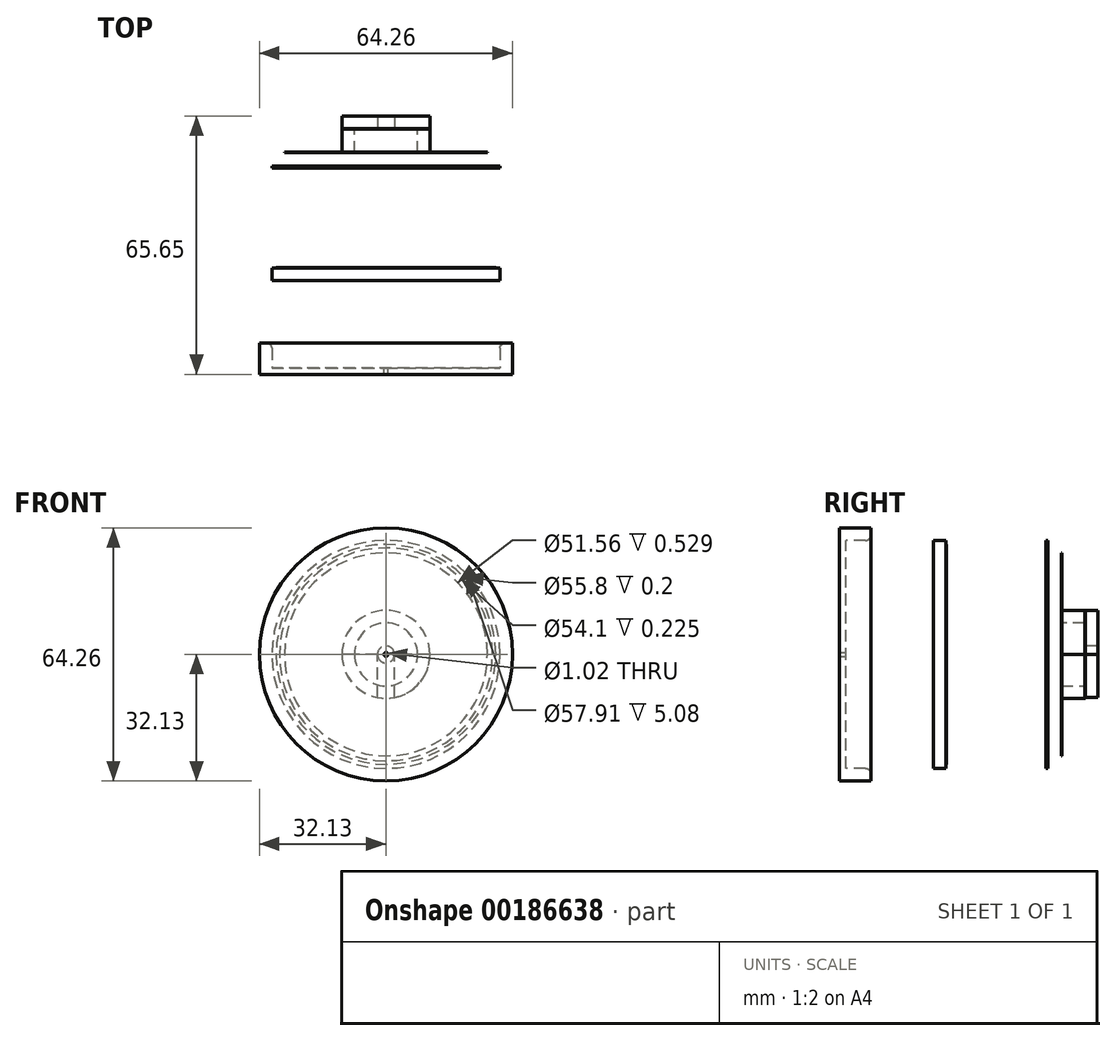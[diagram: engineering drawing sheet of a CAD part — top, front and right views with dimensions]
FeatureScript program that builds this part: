
annotation { "Feature Type Name" : "Feature", "Feature Type Description" : "" }
export const myFeature = defineFeature(function(context is Context, id is Id, definition is map)
    precondition{}
    {
        {
            assignVariable(context, id + "F0", {"name" : "Ant_Thick", "anyValue" : 1 / 8});
        }
        {
            assignVariable(context, id + "F1", {"name" : "SHIELD_Thick", "anyValue" : .1});
        }
        {
            assignVariable(context, id + "F2", {"name" : "tolerance", "anyValue" : 0});
        }
        {
            assignVariable(context, id + "F3", {"name" : "Layers_SH", "anyValue" : 4});
        }
        {
            assignVariable(context, id + "F4", {"name" : "LID_FOLD_DEPTH", "anyValue" : .2});
        }
        {
            assignVariable(context, id + "F5", {"name" : "TOT_SH_SPACE", "anyValue" : getVariable(context, 'SHIELD_Thick') * getVariable(context, 'Layers_SH') + getVariable(context, 'tolerance')});
        }
        {
            var Q0;
            Q0=qCreatedBy(makeId("Front.planeOp"),FACE);
            var sketch = newSketch(context, id + "F6", { "sketchPlane" : qUnion([Q0])});
            skCircle(sketch, "E0", {"center": v(0, 0) * mm, "radius": 25.78 * mm});
            skLineSegment(sketch, "E1", {"start": v(0, 28.96) * mm, "end": v(0, -28.96) * mm, "construction": true});
            skLineSegment(sketch, "E2", {"start": v(28.96, 0) * mm, "end": v(-28.96, 0) * mm, "construction": true});
            skCircle(sketch, "E3.0", {"center": v(0, 0) * mm, "radius": 28.96 * mm});
            skCircle(sketch, "E4", {"center": v(0, 0) * mm, "radius": 24.77 * mm, "construction": true});
            skCircle(sketch, "E5", {"center": v(0, 0) * mm, "radius": 8 * mm});
            skCircle(sketch, "E6", {"center": v(0, 0) * mm, "radius": 6.99 * mm, "construction": true});
            skCircle(sketch, "E7", {"center": v(0, 0) * mm, "radius": 2.16 * mm});
            skCircle(sketch, "E8.0", {"center": v(0, 0) * mm, "radius": 11.18 * mm});
            skLineSegment(sketch, "E9", {"start": v(11.18, 0) * mm, "end": v(-11.18, 0) * mm});
            skCircle(sketch, "E10.0", {"center": v(0, 0) * mm, "radius": 27.05 * mm});
            skCircle(sketch, "E11", {"center": v(0, 0) * mm, "radius": 27.9 * mm});
            skCircle(sketch, "E12", {"center": v(0, 0) * mm, "radius": 27.64 * mm, "construction": true});
            skSolve(sketch);
        }
        {
            var Q0;
            Q0=makeQuery(id+"F6.imprint","IMPRINT",FACE,{"disambiguationData":[TD([[makeQuery(id+"F6.imprint","IMPRINT",EDGE,{"derivedFrom":sQuery(id+"F6.wireOp",EDGE,"E0")}),-1.0]])]});
            var Q1;
            Q1=makeQuery(id+"F6.imprint","IMPRINT",FACE,{"disambiguationData":[TD([[makeQuery(id+"F6.imprint","IMPRINT",EDGE,{"derivedFrom":sQuery(id+"F6.wireOp",EDGE,"E3.0")}),1.0]])]});
            var Q2;
            Q2=makeQuery(id+"F6.imprint","IMPRINT",FACE,{"disambiguationData":[TD([[makeQuery(id+"F6.imprint","IMPRINT",EDGE,{"derivedFrom":sQuery(id+"F6.wireOp",EDGE,"E10.0")}),-1.0]])]});
            extrude(context, id + "F7", {"entities" : qUnion([Q0, Q1, Q2]), "depth" : (3.56 + getVariable(context, 'Ant_Thick') + (getVariable(context, 'Layers_SH') * getVariable(context, 'SHIELD_Thick') + getVariable(context, 'tolerance'))) * mm});
        }
        {
            var Q0;
            {var subQ0=sQuery(id+"F6.wireOp",EDGE,"E9");var subQ1=sQuery(id+"F6.wireOp",EDGE,"E5");var subQ2=makeQuery(id+"F6.imprint","INTERSECT",VERTEX,{"disambiguationData":[OD(0.0)],"derivedFrom":[subQ1,subQ0]});Q0=makeQuery(id+"F6.imprint","IMPRINT",FACE,{"disambiguationData":[TD([[makeQuery(id+"F6.imprint","IMPRINT",EDGE,{"disambiguationData":[TD([[subQ2,1.0]])],"derivedFrom":subQ1}),-1.0]])]});}
            var Q1;
            Q1=makeQuery(id+"F6.imprint","IMPRINT",FACE,{"disambiguationData":[TD([[makeQuery(id+"F6.imprint","IMPRINT",EDGE,{"derivedFrom":sQuery(id+"F6.wireOp",EDGE,"E0")}),-1.0]])]});
            var Q2;
            Q2=makeQuery(id+"F6.imprint","IMPRINT",FACE,{"disambiguationData":[TD([[makeQuery(id+"F6.imprint","IMPRINT",EDGE,{"derivedFrom":sQuery(id+"F6.wireOp",EDGE,"E0")}),1.0]])]});
            extrude(context, id + "F8", {"entities" : qUnion([Q0, Q1, Q2]), "depth" : (getVariable(context, 'Ant_Thick')) * mm});
        }
        {
            var Q0;
            {var subQ0=sQuery(id+"F6.wireOp",EDGE,"E9");var subQ1=sQuery(id+"F6.wireOp",EDGE,"E5");var subQ2=makeQuery(id+"F6.imprint","INTERSECT",VERTEX,{"disambiguationData":[OD(0.0)],"derivedFrom":[subQ1,subQ0]});Q0=makeQuery(id+"F6.imprint","IMPRINT",FACE,{"disambiguationData":[TD([[makeQuery(id+"F6.imprint","IMPRINT",EDGE,{"disambiguationData":[TD([[subQ2,1.0]])],"derivedFrom":subQ1}),-1.0]])]});}
            extrude(context, id + "F9", {"entities" : qUnion([Q0]), "operationType" : NewBodyOperationType.ADD, "oppositeDirection" : true, "depth" : (6 - getVariable(context, 'Ant_Thick')) * mm});
        }
        {
            var Q0;
            Q0=makeQuery(id+"F9.opExtrude","CAP_FACE",FACE,{"disambiguationData":[OSD([sQuery(id+"F6.wireOp",EDGE,"E5"),sQuery(id+"F6.wireOp",EDGE,"E8.0")])],"isStart":false});
            var sketch = newSketch(context, id + "F10", { "sketchPlane" : qUnion([Q0])});
            skCircle(sketch, "E13", {"center": v(0, 0) * mm, "radius": 2.16 * mm});
            skCircle(sketch, "E14", {"center": v(0, 0) * mm, "radius": 8 * mm});
            skCircle(sketch, "E15", {"center": v(0, 0) * mm, "radius": 11.18 * mm});
            skLineSegment(sketch, "E16", {"start": v(-11.18, 0) * mm, "end": v(11.18, 0) * mm});
            skSolve(sketch);
        }
        {
            var Q0;
            {var subQ0=sQuery(id+"F10.wireOp",EDGE,"E14");Q0=makeQuery(id+"F10.imprint","IMPRINT",FACE,{"disambiguationData":[TD([[makeQuery(id+"F10.imprint","IMPRINT",EDGE,{"disambiguationData":[OD(1.0)],"derivedFrom":subQ0}),1.0]])]});}
            var Q1;
            {var subQ4=sQuery(id+"F10.wireOp",EDGE,"E14");Q1=makeQuery(id+"F10.imprint","IMPRINT",FACE,{"disambiguationData":[TD([[makeQuery(id+"F10.imprint","IMPRINT",EDGE,{"disambiguationData":[OD(1.0)],"derivedFrom":subQ4}),-1.0]])]});}
            var Q2;
            {var subQ0=sQuery(id+"F10.wireOp",EDGE,"E14");Q2=makeQuery(id+"F10.imprint","IMPRINT",FACE,{"disambiguationData":[TD([[makeQuery(id+"F10.imprint","IMPRINT",EDGE,{"disambiguationData":[OD(1.0)],"derivedFrom":subQ0}),1.0]])]});}
            extrude(context, id + "F11", {"entities" : qUnion([Q0, Q1, Q2]), "depth" : (getVariable(context, 'Ant_Thick')) * mm});
        }
        {
            var Q0;
            {var subQ0=sQuery(id+"F6.wireOp",EDGE,"E9");var subQ1=sQuery(id+"F6.wireOp",EDGE,"E5");var subQ2=makeQuery(id+"F6.imprint","INTERSECT",VERTEX,{"disambiguationData":[OD(0.0)],"derivedFrom":[subQ1,subQ0]});Q0=makeQuery(id+"F6.imprint","IMPRINT",FACE,{"disambiguationData":[TD([[makeQuery(id+"F6.imprint","IMPRINT",EDGE,{"disambiguationData":[TD([[subQ2,-1.0]])],"derivedFrom":subQ1}),-1.0]])]});}
            var Q1;
            Q1=makeQuery(id+"F9.opExtrude","CAP_FACE",FACE,{"disambiguationData":[OSD([sQuery(id+"F6.wireOp",EDGE,"E5"),sQuery(id+"F6.wireOp",EDGE,"E8.0"),sQuery(id+"F6.wireOp",EDGE,"E9")])],"isStart":false});
            var Q2;
            Q2=makeQuery(id+"F8.opExtrude","CAP_FACE",FACE,{"disambiguationData":[OSD([sQuery(id+"F6.wireOp",EDGE,"E3.0"),sQuery(id+"F6.wireOp",EDGE,"E5"),sQuery(id+"F6.wireOp",EDGE,"E8.0"),sQuery(id+"F6.wireOp",EDGE,"E9")])],"isStart":false});
            extrude(context, id + "F12", {"entities" : qUnion([Q0]), "endBound" : BoundingType.UP_TO_SURFACE, "oppositeDirection" : true, "endBoundEntityFace" : qUnion([Q1]), "depth" : 25.4 * mm, "hasSecondDirection" : true, "secondDirectionBound" : SecondDirectionBoundingType.UP_TO_SURFACE, "secondDirectionOppositeDirection" : false, "secondDirectionBoundEntityFace" : qUnion([Q2]), "secondDirectionDepth" : 25.4 * mm});
        }
        {
            var Q0;
            {var subQ0=sQuery(id+"F10.wireOp",EDGE,"E14");Q0=makeQuery(id+"F10.imprint","IMPRINT",FACE,{"disambiguationData":[TD([[makeQuery(id+"F10.imprint","IMPRINT",EDGE,{"disambiguationData":[OD(0.0)],"derivedFrom":subQ0}),-1.0]])]});}
            var Q1;
            {var subQ4=sQuery(id+"F10.wireOp",EDGE,"E14");Q1=makeQuery(id+"F10.imprint","IMPRINT",FACE,{"disambiguationData":[TD([[makeQuery(id+"F10.imprint","IMPRINT",EDGE,{"disambiguationData":[OD(0.0)],"derivedFrom":subQ4}),1.0]])]});}
            var Q2;
            Q2=makeQuery(id+"F11.opExtrude","CAP_FACE",FACE,{"disambiguationData":[OSD([sQuery(id+"F10.wireOp",EDGE,"E13"),sQuery(id+"F10.wireOp",EDGE,"E15"),sQuery(id+"F10.wireOp",EDGE,"E16")])],"isStart":false});
            extrude(context, id + "F13", {"entities" : qUnion([Q0, Q1]), "endBoundEntityFace" : qUnion([Q2]), "depth" : (getVariable(context, 'Ant_Thick')) * mm});
        }
        {
            var Q0;
            Q0=makeQuery(id+"F13.opExtrude","CAP_FACE",FACE,{"disambiguationData":[OSD([sQuery(id+"F10.wireOp",EDGE,"E13"),sQuery(id+"F10.wireOp",EDGE,"E15"),sQuery(id+"F10.wireOp",EDGE,"E16")])],"isStart":false});
            extrude(context, id + "F14", {"entities" : qUnion([Q0]), "depth" : 3.17 * mm});
        }
        {
            var Q0;
            {var subQ0=sQuery(id+"F10.wireOp",EDGE,"E16");var subQ1=makeQuery(id+"F10.imprint","INTERSECT",VERTEX,{"disambiguationData":[OD(1.0)],"derivedFrom":[sQuery(id+"F10.wireOp",EDGE,"E14"),subQ0]});Q0=makeQuery(id+"F14.opExtrude","SWEPT_FACE",FACE,{"disambiguationData":[OSD([subQ0]),TDD([makeQuery(id+"F13.opExtrude","CAP_EDGE",EDGE,{"disambiguationData":[OSD([subQ0]),TDD([makeQuery(id+"F10.imprint","IMPRINT",EDGE,{"disambiguationData":[TD([[subQ1,1.0]])],"derivedFrom":subQ0}),makeQuery(id+"F10.imprint","IMPRINT",EDGE,{"disambiguationData":[TD([[makeQuery(id+"F10.imprint","INTERSECT",VERTEX,{"disambiguationData":[OD(1.0)],"derivedFrom":[sQuery(id+"F10.wireOp",EDGE,"E15"),subQ0]}),1.0]])],"derivedFrom":subQ0})])],"isStart":false})])]});}
            var Q1;
            {var subQ0=sQuery(id+"F10.wireOp",EDGE,"E16");var subQ1=makeQuery(id+"F10.imprint","INTERSECT",VERTEX,{"disambiguationData":[OD(0.0)],"derivedFrom":[sQuery(id+"F10.wireOp",EDGE,"E14"),subQ0]});Q1=makeQuery(id+"F14.opExtrude","SWEPT_FACE",FACE,{"disambiguationData":[OSD([subQ0]),TDD([makeQuery(id+"F13.opExtrude","CAP_EDGE",EDGE,{"disambiguationData":[OSD([subQ0]),TDD([makeQuery(id+"F10.imprint","IMPRINT",EDGE,{"disambiguationData":[TD([[makeQuery(id+"F10.imprint","INTERSECT",VERTEX,{"disambiguationData":[OD(0.0)],"derivedFrom":[sQuery(id+"F10.wireOp",EDGE,"E15"),subQ0]}),-1.0]])],"derivedFrom":subQ0}),makeQuery(id+"F10.imprint","IMPRINT",EDGE,{"disambiguationData":[TD([[subQ1,-1.0]])],"derivedFrom":subQ0})])],"isStart":false})])]});}
            var Q2;
            Q2=makeQuery(id+"F11.opExtrude","SWEPT_FACE",FACE,{"disambiguationData":[OSD([sQuery(id+"F10.wireOp",EDGE,"E15")])]});
            extrude(context, id + "F15", {"entities" : qUnion([Q0, Q1]), "endBound" : BoundingType.UP_TO_SURFACE, "endBoundEntityFace" : qUnion([Q2]), "depth" : 25.4 * mm});
        }
        {
            var Q0;
            Q0=qCreatedBy(makeId("Front.planeOp"),FACE);
            cPlane(context, id + "F16", {"entities" : qUnion([Q0]), "cplaneType" : CPlaneType.OFFSET, "offset" : (getVariable(context, 'Ant_Thick')) * mm, "width" : 152.4 * mm, "height" : 152.4 * mm});
        }
        {
            var Q0;
            Q0=makeQuery(id+"F7.opExtrude","CAP_FACE",FACE,{"disambiguationData":[OSD([sQuery(id+"F6.wireOp",EDGE,"E0"),sQuery(id+"F6.wireOp",EDGE,"E3.0")])],"isStart":false});
            cPlane(context, id + "F17", {"entities" : qUnion([Q0]), "cplaneType" : CPlaneType.OFFSET, "offset" : 25.4 * mm, "width" : 152.4 * mm, "height" : 152.4 * mm});
        }
        {
            var Q0;
            Q0=qCreatedBy(id+"F17.planeOp",FACE);
            var sketch = newSketch(context, id + "F18", { "sketchPlane" : qUnion([Q0])});
            skCircle(sketch, "E17", {"center": v(0, 0) * mm, "radius": 28.96 * mm});
            skCircle(sketch, "E18", {"center": v(0, 0) * mm, "radius": 24.77 * mm});
            skCircle(sketch, "E19", {"center": v(0, 0) * mm, "radius": 27.9 * mm});
            skCircle(sketch, "E20", {"center": v(0, 0) * mm, "radius": 27.05 * mm});
            skSolve(sketch);
        }
        {
            var Q0;
            Q0=makeQuery(id+"F18.imprint","IMPRINT",FACE,{"disambiguationData":[TD([[makeQuery(id+"F18.imprint","IMPRINT",EDGE,{"derivedFrom":sQuery(id+"F18.wireOp",EDGE,"E17")}),1.0]])]});
            var Q1;
            Q1=makeQuery(id+"F18.imprint","IMPRINT",FACE,{"disambiguationData":[TD([[makeQuery(id+"F18.imprint","IMPRINT",EDGE,{"derivedFrom":sQuery(id+"F18.wireOp",EDGE,"E18")}),1.0]])]});
            var Q2;
            Q2=makeQuery(id+"F18.imprint","IMPRINT",FACE,{"disambiguationData":[TD([[makeQuery(id+"F18.imprint","IMPRINT",EDGE,{"derivedFrom":sQuery(id+"F18.wireOp",EDGE,"E18")}),-1.0]])]});
            var Q3;
            Q3=makeQuery(id+"F18.imprint","IMPRINT",FACE,{"disambiguationData":[TD([[makeQuery(id+"F18.imprint","IMPRINT",EDGE,{"derivedFrom":sQuery(id+"F18.wireOp",EDGE,"E19")}),1.0]])]});
            extrude(context, id + "F19", {"entities" : qUnion([Q0, Q1, Q2, Q3]), "depth" : 3.17 * mm});
        }
        {
            var Q0;
            Q0=makeQuery(id+"F18.imprint","IMPRINT",FACE,{"disambiguationData":[TD([[makeQuery(id+"F18.imprint","IMPRINT",EDGE,{"derivedFrom":sQuery(id+"F18.wireOp",EDGE,"E18")}),1.0]])]});
            var Q1;
            Q1=makeQuery(id+"F18.imprint","IMPRINT",FACE,{"disambiguationData":[TD([[makeQuery(id+"F18.imprint","IMPRINT",EDGE,{"derivedFrom":sQuery(id+"F18.wireOp",EDGE,"E18")}),-1.0]])]});
            extrude(context, id + "F20", {"entities" : qUnion([Q0, Q1]), "oppositeDirection" : true, "depth" : (getVariable(context, 'Ant_Thick')) * mm});
        }
        {
            var Q0;
            Q0=makeQuery(id+"F7.opExtrude","CAP_FACE",FACE,{"disambiguationData":[OSD([sQuery(id+"F6.wireOp",EDGE,"E0"),sQuery(id+"F6.wireOp",EDGE,"E3.0")])],"isStart":false});
            var sketch = newSketch(context, id + "F21", { "sketchPlane" : qUnion([Q0])});
            skCircle(sketch, "E21", {"center": v(0, 0) * mm, "radius": 27.05 * mm});
            skCircle(sketch, "E22", {"center": v(0, 0) * mm, "radius": 27.64 * mm});
            skCircle(sketch, "E23", {"center": v(0, 0) * mm, "radius": 27.9 * mm});
            skSolve(sketch);
        }
        {
            var Q0;
            Q0=makeQuery(id+"F21.imprint","IMPRINT",FACE,{"disambiguationData":[TD([[makeQuery(id+"F21.imprint","IMPRINT",EDGE,{"derivedFrom":sQuery(id+"F21.wireOp",EDGE,"E22")}),-1.0]])]});
            var Q1;
            Q1=makeQuery(id+"F21.imprint","IMPRINT",FACE,{"disambiguationData":[TD([[makeQuery(id+"F21.imprint","IMPRINT",EDGE,{"derivedFrom":sQuery(id+"F21.wireOp",EDGE,"E21")}),-1.0]])]});
            extrude(context, id + "F22", {"entities" : qUnion([Q0, Q1]), "operationType" : NewBodyOperationType.REMOVE, "oppositeDirection" : true, "depth" : (getVariable(context, 'LID_FOLD_DEPTH')) * mm});
        }
        {
            var Q0;
            Q0=makeQuery(id+"F18.imprint","IMPRINT",FACE,{"disambiguationData":[TD([[makeQuery(id+"F18.imprint","IMPRINT",EDGE,{"derivedFrom":sQuery(id+"F18.wireOp",EDGE,"E19")}),1.0]])]});
            extrude(context, id + "F23", {"entities" : qUnion([Q0]), "oppositeDirection" : true, "depth" : (getVariable(context, 'Ant_Thick') + .1) * mm});
        }
        {
            var Q0;
            Q0=qCreatedBy(id+"F16.planeOp",FACE);
            var sketch = newSketch(context, id + "F24", { "sketchPlane" : qUnion([Q0])});
            skCircle(sketch, "E24", {"center": v(0, 0) * mm, "radius": 27.9 * mm});
            skCircle(sketch, "E25", {"center": v(0, 0) * mm, "radius": 25.78 * mm});
            skCircle(sketch, "E26", {"center": v(0, 0) * mm, "radius": 27.05 * mm});
            skSolve(sketch);
        }
        {
            var Q0;
            Q0=makeQuery(id+"F24.imprint","IMPRINT",FACE,{"disambiguationData":[TD([[makeQuery(id+"F24.imprint","IMPRINT",EDGE,{"derivedFrom":sQuery(id+"F24.wireOp",EDGE,"E25")}),-1.0]])]});
            extrude(context, id + "F25", {"entities" : qUnion([Q0]), "operationType" : NewBodyOperationType.REMOVE, "depth" : (getVariable(context, 'TOT_SH_SPACE')) * mm});
        }
        {
            var Q0;
            Q0 = qSketchRegion(id + "F24", true);
            extrude(context, id + "F26", {"entities" : qUnion([Q0]), "operationType" : NewBodyOperationType.REMOVE, "depth" : (getVariable(context, 'LID_FOLD_DEPTH')) * mm});
        }
        {
            var Q0;
            Q0=makeQuery(id+"F26.boolean.opBoolean","COPY",EDGE,{"derivedFrom":makeQuery(id+"F26.opExtrude","CAP_EDGE",EDGE,{"disambiguationData":[OSD([sQuery(id+"F24.wireOp",EDGE,"E24")])],"isStart":true})});
            fillet(context, id + "F27", {"entities" : qUnion([Q0]), "radius" : 1.27 * mm, "tangentPropagation" : true, "allowEdgeOverflow" : false});
        }
        {
            var Q0;
            Q0=qCreatedBy(id+"F17.planeOp",FACE);
            cPlane(context, id + "F28", {"entities" : qUnion([Q0]), "cplaneType" : CPlaneType.OFFSET, "offset" : 25.4 * mm, "width" : 152.4 * mm, "height" : 152.4 * mm});
        }
        {
            var Q0;
            Q0=makeQuery(id+"F22.boolean.opBoolean","COPY",EDGE,{"derivedFrom":makeQuery(id+"F22.opExtrude","CAP_EDGE",EDGE,{"disambiguationData":[OSD([sQuery(id+"F21.wireOp",EDGE,"E21")])],"isStart":true})});
            fillet(context, id + "F29", {"entities" : qUnion([Q0]), "radius" : 1.27 * mm, "tangentPropagation" : true, "allowEdgeOverflow" : false});
        }
        {
            var Q0;
            Q0=qCreatedBy(id+"F28.planeOp",FACE);
            var sketch = newSketch(context, id + "F30", { "sketchPlane" : qUnion([Q0])});
            skCircle(sketch, "E27", {"center": v(0, 0) * mm, "radius": 28.96 * mm});
            skCircle(sketch, "E28.0", {"center": v(0, 0) * mm, "radius": 32.13 * mm});
            skCircle(sketch, "E29", {"center": v(0, 0) * mm, "radius": 0.5 * mm});
            skSolve(sketch);
        }
        {
            var Q0;
            Q0=makeQuery(id+"F30.imprint","IMPRINT",FACE,{"disambiguationData":[TD([[makeQuery(id+"F30.imprint","IMPRINT",EDGE,{"derivedFrom":sQuery(id+"F30.wireOp",EDGE,"E27")}),1.0]])]});
            var Q1;
            Q1=makeQuery(id+"F30.imprint","IMPRINT",FACE,{"disambiguationData":[TD([[makeQuery(id+"F30.imprint","IMPRINT",EDGE,{"derivedFrom":sQuery(id+"F30.wireOp",EDGE,"E27")}),-1.0]])]});
            extrude(context, id + "F31", {"entities" : qUnion([Q0, Q1]), "depth" : 1.59 * mm});
        }
        {
            var Q0;
            Q0=makeQuery(id+"F30.imprint","IMPRINT",FACE,{"disambiguationData":[TD([[makeQuery(id+"F30.imprint","IMPRINT",EDGE,{"derivedFrom":sQuery(id+"F30.wireOp",EDGE,"E27")}),-1.0]])]});
            extrude(context, id + "F32", {"entities" : qUnion([Q0]), "operationType" : NewBodyOperationType.ADD, "oppositeDirection" : true, "depth" : 6.35 * mm});
        }
        {
            var Q0;
            Q0=makeQuery(id+"F32.opExtrude","CAP_EDGE",EDGE,{"disambiguationData":[OSD([sQuery(id+"F30.wireOp",EDGE,"E27")])],"isStart":false});
            fillet(context, id + "F33", {"entities" : qUnion([Q0]), "radius" : 1.27 * mm, "tangentPropagation" : true, "allowEdgeOverflow" : false});
        }
        {
            var Q0;
            Q0=makeQuery(id+"F25.boolean.opBoolean","COPY",EDGE,{"derivedFrom":makeQuery(id+"F25.opExtrude","CAP_EDGE",EDGE,{"disambiguationData":[OSD([sQuery(id+"F24.wireOp",EDGE,"E26")])],"isStart":false})});
            fillet(context, id + "F34", {"entities" : qUnion([Q0]), "radius" : 1.27 * mm, "tangentPropagation" : true, "allowEdgeOverflow" : false});
        }
        {
            var Q0;
            Q0=qCreatedBy(makeId("Right.planeOp"),FACE);
            var sketch = newSketch(context, id + "F35", { "sketchPlane" : qUnion([Q0])});
            skLineSegment(sketch, "E30.bottom", {"start": v(-8.82, 21.88) * mm, "end": v(-28.9, 21.88) * mm});
            skLineSegment(sketch, "E30.top", {"start": v(-8.82, -21.78) * mm, "end": v(-28.9, -21.78) * mm});
            skLineSegment(sketch, "E30.left", {"start": v(-8.82, 21.88) * mm, "end": v(-8.82, -21.78) * mm});
            skLineSegment(sketch, "E30.right", {"start": v(-28.9, 21.88) * mm, "end": v(-28.9, -21.78) * mm});
            skSolve(sketch);
        }
        {
            var Q0;
            Q0 = qSketchRegion(id + "F35", true);
            extrude(context, id + "F36", {"entities" : qUnion([Q0]), "operationType" : NewBodyOperationType.REMOVE, "endBound" : BoundingType.SYMMETRIC, "depth" : 76.2 * mm});
        }
        {
            var Q0;
            Q0=makeQuery(id+"F6.imprint","IMPRINT",FACE,{"disambiguationData":[TD([[makeQuery(id+"F6.imprint","IMPRINT",EDGE,{"derivedFrom":sQuery(id+"F6.wireOp",EDGE,"E0")}),-1.0]])]});
            var Q1;
            Q1=makeQuery(id+"F6.imprint","IMPRINT",FACE,{"disambiguationData":[TD([[makeQuery(id+"F6.imprint","IMPRINT",EDGE,{"derivedFrom":sQuery(id+"F6.wireOp",EDGE,"E10.0")}),-1.0]])]});
            var Q2;
            Q2=makeQuery(id+"F6.imprint","IMPRINT",FACE,{"disambiguationData":[TD([[makeQuery(id+"F6.imprint","IMPRINT",EDGE,{"derivedFrom":sQuery(id+"F6.wireOp",EDGE,"E3.0")}),1.0]])]});
            extrude(context, id + "F37", {"entities" : qUnion([Q0, Q1, Q2]), "operationType" : NewBodyOperationType.REMOVE, "depth" : 3.56 * mm});
        }
    });
